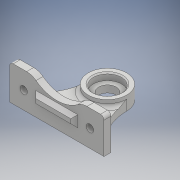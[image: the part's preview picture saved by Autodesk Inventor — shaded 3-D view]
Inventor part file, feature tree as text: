
AUTODESK INVENTOR PART (.ipt)
format: ipt  version: 2018 (Build 220112000, 112)  size: 207,872 bytes
history: native  units: mm
features: extrude x6, sketch x6, fillet x2, chamfer x2
ambient origin geometry x8: Origin, YZ Plane, XZ Plane, XY Plane, X Axis, Y Axis, Z Axis, Center Point
bodies: Solid1 (feature_tree)
feature tree (16):
  extrude  "Extrusion1"  Depth=10.0mm
  extrude  "Extrusion2"  Depth=4.0mm
  extrude  "Extrusion3"  Depth=4.0mm TaperAngle=0.0deg
  extrude  "Extrusion4"  Depth=4.0mm TaperAngle=0.0deg
  fillet  "Fillet1"  Radius=16.0mm
  chamfer  "Chamfer1"  Distance=8.0mm
  extrude  "Extrusion5"  Depth=9.0mm
  chamfer  "Chamfer2"  Distance=16.0mm
  extrude  "Extrusion6"  Depth=2.0mm
  fillet  "Fillet2"  Radius=2.0mm
  sketch  "Sketch1"  dims[d0=10.0mm d1=22.0mm]
  sketch  "Sketch2"  dims[d2=4.0mm d3=27.0mm]
  sketch  "Sketch3"  dims[d4=25.0mm d5=4.0mm d6=0.0mm]
  sketch  "Sketch4"  dims[d7=16.0mm d8=4.0mm d9=0.0mm d10=16.0mm d11=0.0mm]
  sketch  "Sketch5"  dims[d12=4.2mm]
  sketch  "Sketch6"  dims[d13=10.0mm d14=8.0mm d15=8.0mm d16=16.0mm d17=0.0mm d18=2.0mm d19=0.7mm d20=2.0mm d21=45.0deg d22=2.5mm d23=20.0mm d24=2.0mm d25=0.0mm d26=2.0mm d27=2.0mm d28=45.0deg d29=20.0mm d30=14.0mm d31=2.0mm d32=0.0mm d33=9.0mm]
